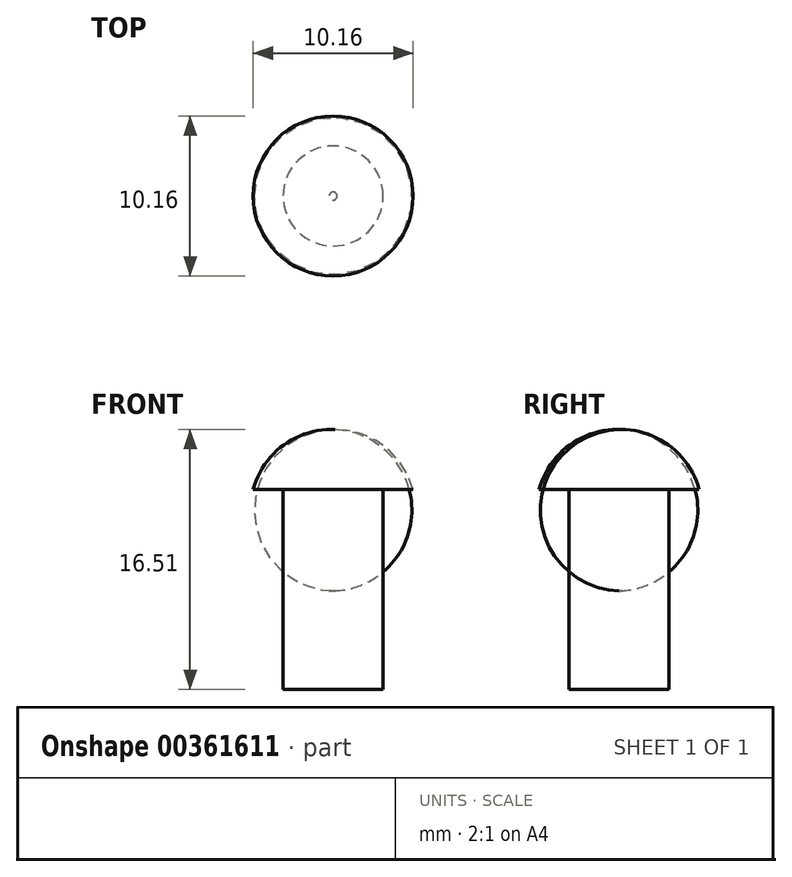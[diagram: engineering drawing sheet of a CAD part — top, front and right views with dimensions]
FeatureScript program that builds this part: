
annotation { "Feature Type Name" : "Feature", "Feature Type Description" : "" }
export const myFeature = defineFeature(function(context is Context, id is Id, definition is map)
    precondition{}
    {
        {
            var Q0;
            Q0=qCreatedBy(makeId("Front.planeOp"),FACE);
            var sketch = newSketch(context, id + "F0", { "sketchPlane" : qUnion([Q0])});
            skLineSegment(sketch, "E0.left", {"start": v(3.18, 6.35) * mm, "end": v(3.18, -6.35) * mm});
            skPoint(sketch, "E0.middle", {"position": v(0, 0) * mm});
            skLineSegment(sketch, "E1", {"start": v(3.18, 6.35) * mm, "end": v(5.08, 6.35) * mm});
            skPoint(sketch, "E2", {"position": v(0, 10.16) * mm});
            skLineSegment(sketch, "E3", {"start": v(0, 10.16) * mm, "end": v(0, -6.35) * mm});
            skLineSegment(sketch, "E4", {"start": v(3.18, -6.35) * mm, "end": v(0, -6.35) * mm});
            skArc(sketch, "E5", {"start": v(5.08, 6.35) * mm, "mid": v(3.2, 9.14) * mm, "end": v(0, 10.16) * mm});
            skSolve(sketch);
        }
        {
            var Q0;
            Q0 = qSketchRegion(id + "F0", true);
            var Q1;
            Q1=sQuery(id+"F0.wireOp",EDGE,"E3");
            revolve(context, id + "F1", {"entities" : qUnion([Q0]), "axis" : qUnion([Q1]), "revolveType" : RevolveType.FULL});
        }
    });
